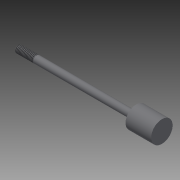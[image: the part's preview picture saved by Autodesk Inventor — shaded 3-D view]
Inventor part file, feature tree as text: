
AUTODESK INVENTOR PART (.ipt)
format: ipt  version: 2014 (Build 180170000, 170)  size: 125,952 bytes
history: native  units: in
note: dims shown in document units (in); Inventor stores cm internally (conversion verified against a paired STEP export)
features: other x49, revolve x3, sketch x3, thread x1
ambient origin geometry x8: Origin, YZ Plane, XZ Plane, XY Plane, X Axis, Y Axis, Z Axis, Center Point
bodies: Solid1 (feature_tree)
feature tree (56):
  revolve  "Revolution1"  [1 undecoded]
  thread  "Thread1"  [1 undecoded]
  revolve  "Revolution2"  [1 undecoded]
  revolve  "Revolution3"  [1 undecoded]
  other  "h1_XY"
  other  "h1_YZ"
  other  "h1_ZX"
  other  "h1_X"
  other  "h1_Y"
  other  "h1_Z"
  other  "h1_Center"
  other  "h2_XY"
  other  "h2_YZ"
  other  "h2_ZX"
  other  "h2_X"
  other  "h2_Y"
  other  "h2_Z"
  other  "h2_Center"
  other  "k1_XY"
  other  "k1_YZ"
  other  "k1_ZX"
  other  "k1_X"
  other  "k1_Y"
  other  "k1_Z"
  other  "k1_Center"
  other  "k2_XY"
  other  "k2_YZ"
  other  "k2_ZX"
  other  "k2_X"
  other  "k2_Y"
  other  "k2_Z"
  other  "k2_Center"
  other  "start_XY"
  other  "start_YZ"
  other  "start_ZX"
  other  "start_X"
  other  "start_Y"
  other  "start_Z"
  other  "start_Center"
  other  "to_prc_XY"
  other  "to_prc_YZ"
  other  "to_prc_ZX"
  other  "to_prc_X"
  other  "to_prc_Y"
  other  "to_prc_Z"
  other  "to_prc_Center"
  other  "to_rod_guide_XY"
  other  "to_rod_guide_YZ"
  other  "to_rod_guide_ZX"
  other  "to_rod_guide_X"
  other  "to_rod_guide_Y"
  other  "to_rod_guide_Z"
  other  "to_rod_guide_Center"
  sketch  "Sketch_3"  dims[d0=360.0deg d1=0.49in d2=3.291in d3=360.0deg]
  sketch  "Sketch_17"
  sketch  "Sketch_12"  dims[d4=360.0deg]
note: 4 required parameter values undecoded (feature->parameter linkage not recoverable at this tier; creation-order binding heuristic only, values carry confidence <= 0.55)